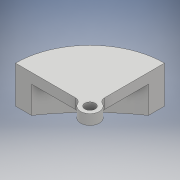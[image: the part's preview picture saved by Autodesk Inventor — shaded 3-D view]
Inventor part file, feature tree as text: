
AUTODESK INVENTOR PART (.ipt)
format: ipt  version: 2018 (Build 220112000, 112)  size: 128,512 bytes
history: native  units: mm
features: sketch x3, extrude x3, plane x1
ambient origin geometry x8: Origin, YZ Plane, XZ Plane, XY Plane, X Axis, Y Axis, Z Axis, Center Point
bodies: Body1 (feature_tree)
feature tree (7):
  sketch  "Sketch1"  dims[d0=44.0mm d4=16.0mm]
  plane  "Work Plane1"
  extrude  "Extrusion3"  Depth=16.0mm
  extrude  "Extrusion4"  Depth=11.0mm
  extrude  "Extrusion5"  Depth=2.0mm
  sketch  "Sketch5"  dims[d23=11.0mm d24=0.0mm d25=3.05mm]
  sketch  "Sketch6"  dims[d26=5.5mm d27=2.0mm d28=3.0mm d29=0.0mm d30=45.0deg d31=5.6mm d32=17.25mm d33=3.0mm d34=0.0mm]
